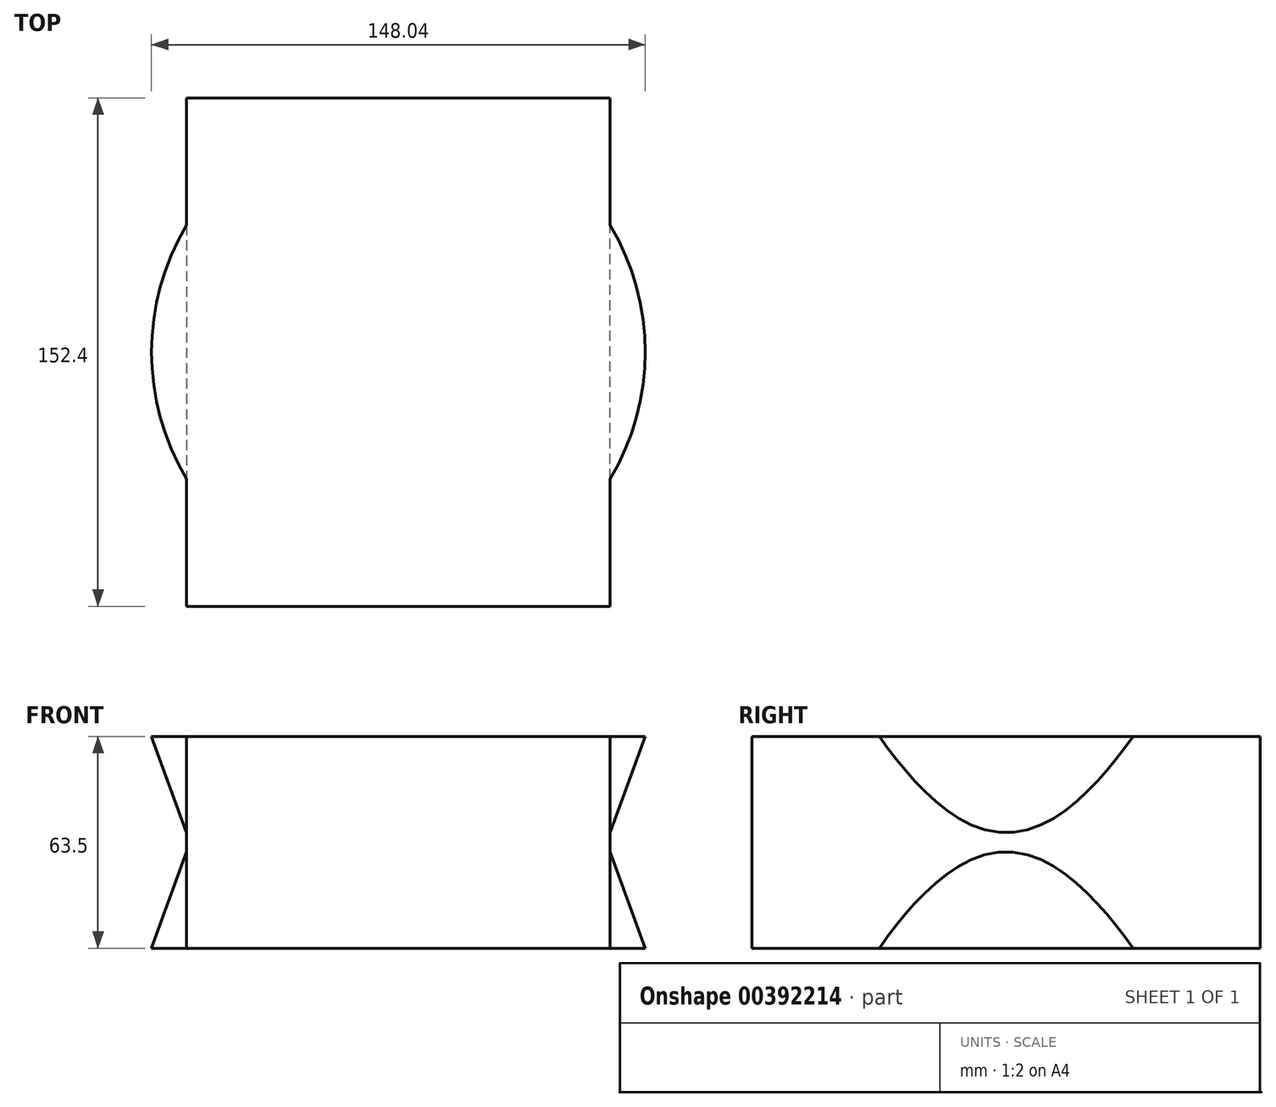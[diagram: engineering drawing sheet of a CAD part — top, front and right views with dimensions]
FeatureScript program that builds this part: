
annotation { "Feature Type Name" : "Feature", "Feature Type Description" : "" }
export const myFeature = defineFeature(function(context is Context, id is Id, definition is map)
    precondition{}
    {
        {
            var Q0;
            Q0=qCreatedBy(makeId("Top.planeOp"),FACE);
            var sketch = newSketch(context, id + "F0", { "sketchPlane" : qUnion([Q0])});
            skLineSegment(sketch, "E0", {"start": v(-63.5, 76.2) * mm, "end": v(-63.5, -76.2) * mm});
            skLineSegment(sketch, "E1", {"start": v(63.5, -76.2) * mm, "end": v(63.5, 76.2) * mm});
            skLineSegment(sketch, "E2", {"start": v(-63.5, -76.2) * mm, "end": v(63.5, -76.2) * mm});
            skLineSegment(sketch, "E3", {"start": v(63.5, 76.2) * mm, "end": v(-63.5, 76.2) * mm});
            skCircle(sketch, "E4", {"center": v(0, 0) * mm, "radius": 62.47 * mm});
            skSolve(sketch);
        }
        {
            var Q0;
            Q0=makeQuery(id+"F0.imprint","IMPRINT",FACE,{"disambiguationData":[TD([[makeQuery(id+"F0.imprint","IMPRINT",EDGE,{"derivedFrom":sQuery(id+"F0.wireOp",EDGE,"E0")}),1.0]])]});
            extrude(context, id + "F1", {"entities" : qUnion([Q0]), "endBound" : BoundingType.SYMMETRIC, "depth" : 63.5 * mm, "offsetDistance" : 25.4 * mm});
        }
        {
            var Q0;
            Q0=makeQuery(id+"F0.imprint","IMPRINT",FACE,{"disambiguationData":[TD([[makeQuery(id+"F0.imprint","IMPRINT",EDGE,{"derivedFrom":sQuery(id+"F0.wireOp",EDGE,"E4")}),1.0]])]});
            extrude(context, id + "F2", {"entities" : qUnion([Q0]), "operationType" : NewBodyOperationType.ADD, "endBound" : BoundingType.SYMMETRIC, "depth" : 63.5 * mm, "offsetDistance" : 25.4 * mm, "hasDraft" : true, "draftAngle" : 20 * degree});
        }
    });
